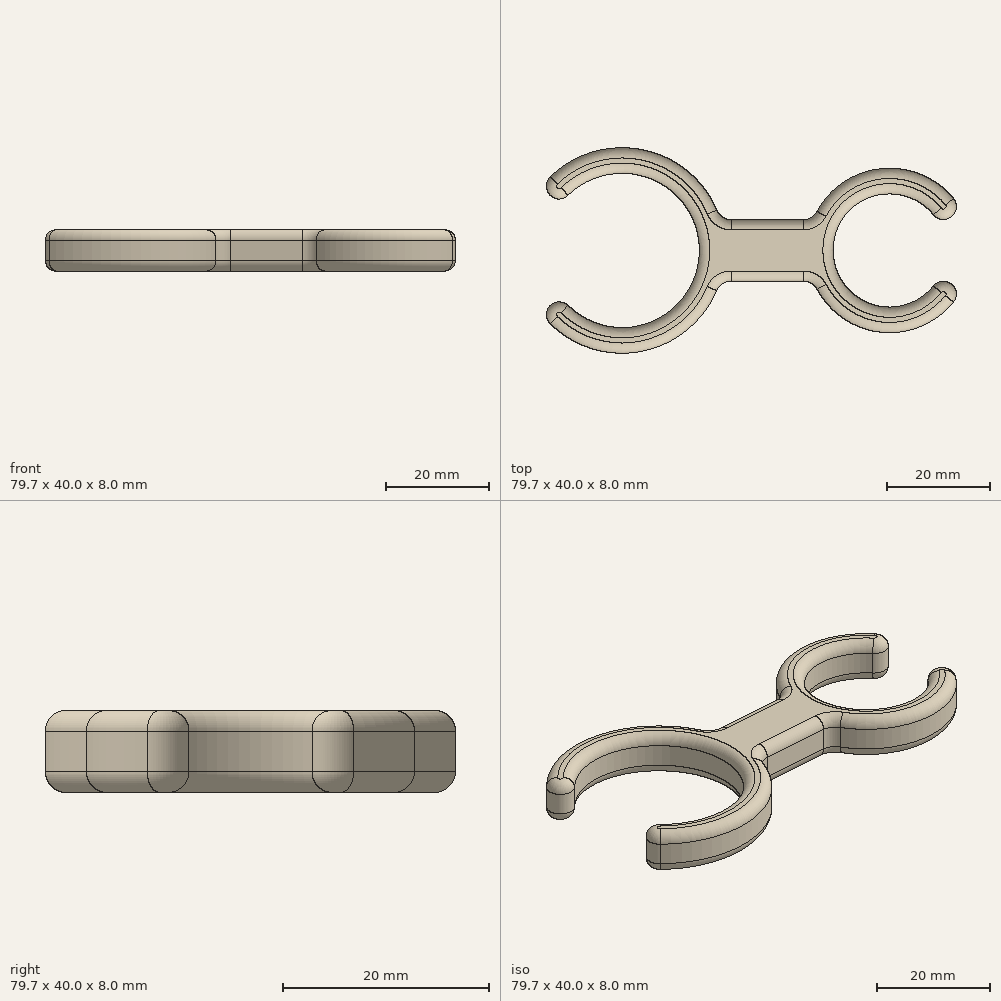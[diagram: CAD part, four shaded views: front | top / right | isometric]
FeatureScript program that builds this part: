
annotation { "Feature Type Name" : "Feature", "Feature Type Description" : "" }
export const myFeature = defineFeature(function(context is Context, id is Id, definition is map)
    precondition{}
    {
        {
            assignVariable(context, id + "F0", {"name" : "ht", "anyValue" : 8});
        }
        {
            var Q0;
            Q0=qCreatedBy(makeId("Top.planeOp"),FACE);
            var sketch = newSketch(context, id + "F1", { "sketchPlane" : qUnion([Q0])});
            skArc(sketch, "E0", {"start": v(-10.5, -10.71) * mm, "mid": v(15, 0) * mm, "end": v(-10.5, 10.71) * mm});
            skArc(sketch, "E1", {"start": v(60.55, 6.93) * mm, "mid": v(41, 0) * mm, "end": v(60.55, -6.93) * mm});
            skLineSegment(sketch, "E2", {"start": v(0, 0) * mm, "end": v(52, 0) * mm, "construction": true});
            skLineSegment(sketch, "E3", {"start": v(19.08, 6) * mm, "end": v(37.17, 6) * mm});
            skLineSegment(sketch, "E4.MirrorCS", {"start": v(19.08, -6) * mm, "end": v(37.17, -6) * mm});
            skArc(sketch, "E5", {"start": v(-14, -14.29) * mm, "mid": v(4.86, -19.4) * mm, "end": v(19.08, -6) * mm});
            skArc(sketch, "E6", {"start": v(64.43, 10.07) * mm, "mid": v(49.64, 15.82) * mm, "end": v(37.17, 6) * mm});
            skArc(sketch, "E7", {"start": v(-14, 14.29) * mm, "mid": v(-14.03, 10.75) * mm, "end": v(-10.5, 10.71) * mm});
            skArc(sketch, "E8.MirrorC", {"start": v(-14, -14.29) * mm, "mid": v(-14.03, -10.75) * mm, "end": v(-10.5, -10.71) * mm});
            skArc(sketch, "E9.trimOffspring", {"start": v(19.08, 6) * mm, "mid": v(4.86, 19.4) * mm, "end": v(-14, 14.29) * mm});
            skPoint(sketch, "E10.orphan", {"position": v(13.75, 6) * mm});
            skPoint(sketch, "E11.orphan", {"position": v(13.75, -6) * mm});
            skArc(sketch, "E12", {"start": v(60.55, 6.93) * mm, "mid": v(64.06, 6.56) * mm, "end": v(64.43, 10.07) * mm});
            skArc(sketch, "E13.MirrorC", {"start": v(60.55, -6.93) * mm, "mid": v(64.06, -6.56) * mm, "end": v(64.43, -10.07) * mm});
            skArc(sketch, "E14.trimOffspring", {"start": v(37.17, -6) * mm, "mid": v(49.64, -15.82) * mm, "end": v(64.43, -10.07) * mm});
            skPoint(sketch, "E15.orphan", {"position": v(42.78, 6) * mm});
            skPoint(sketch, "E16.orphan", {"position": v(42.78, -6) * mm});
            skSolve(sketch);
        }
        {
            var Q0;
            Q0=makeQuery(id+"F1.imprint","IMPRINT",FACE,{"disambiguationData":[TD([[makeQuery(id+"F1.imprint","IMPRINT",EDGE,{"derivedFrom":sQuery(id+"F1.wireOp",EDGE,"E0")}),-1.0]])]});
            extrude(context, id + "F2", {"entities" : qUnion([Q0]), "depth" : (getVariable(context, 'ht')) * mm});
        }
        {
            var Q0;
            Q0=makeQuery(id+"F2.opExtrude","SWEPT_EDGE",EDGE,{"disambiguationData":[OSD([sQuery(id+"F1.wireOp",EDGE,"E4.MirrorCS"),sQuery(id+"F1.wireOp",EDGE,"E5")])]});
            var Q1;
            Q1=makeQuery(id+"F2.opExtrude","SWEPT_EDGE",EDGE,{"disambiguationData":[OSD([sQuery(id+"F1.wireOp",EDGE,"E4.MirrorCS"),sQuery(id+"F1.wireOp",EDGE,"E14.trimOffspring")])]});
            var Q2;
            Q2=makeQuery(id+"F2.opExtrude","SWEPT_EDGE",EDGE,{"disambiguationData":[OSD([sQuery(id+"F1.wireOp",EDGE,"E3"),sQuery(id+"F1.wireOp",EDGE,"E9.trimOffspring")])]});
            var Q3;
            Q3=makeQuery(id+"F2.opExtrude","SWEPT_EDGE",EDGE,{"disambiguationData":[OSD([sQuery(id+"F1.wireOp",EDGE,"E3"),sQuery(id+"F1.wireOp",EDGE,"E6")])]});
            fillet(context, id + "F3", {"entities" : qUnion([Q0, Q1, Q2, Q3]), "radius" : 3 * mm, "tangentPropagation" : true, "allowEdgeOverflow" : false});
        }
        {
            var Q0;
            Q0=makeQuery(id+"F2.opExtrude","CAP_FACE",FACE,{"disambiguationData":[OSD([sQuery(id+"F1.wireOp",EDGE,"E0"),sQuery(id+"F1.wireOp",EDGE,"E1"),sQuery(id+"F1.wireOp",EDGE,"E3"),sQuery(id+"F1.wireOp",EDGE,"E4.MirrorCS"),sQuery(id+"F1.wireOp",EDGE,"E5"),sQuery(id+"F1.wireOp",EDGE,"E6"),sQuery(id+"F1.wireOp",EDGE,"E7"),sQuery(id+"F1.wireOp",EDGE,"E8.MirrorC"),sQuery(id+"F1.wireOp",EDGE,"E9.trimOffspring"),sQuery(id+"F1.wireOp",EDGE,"E12"),sQuery(id+"F1.wireOp",EDGE,"E13.MirrorC"),sQuery(id+"F1.wireOp",EDGE,"E14.trimOffspring")])],"isStart":false});
            var Q1;
            Q1=makeQuery(id+"F2.opExtrude","CAP_FACE",FACE,{"disambiguationData":[OSD([sQuery(id+"F1.wireOp",EDGE,"E0"),sQuery(id+"F1.wireOp",EDGE,"E1"),sQuery(id+"F1.wireOp",EDGE,"E3"),sQuery(id+"F1.wireOp",EDGE,"E4.MirrorCS"),sQuery(id+"F1.wireOp",EDGE,"E5"),sQuery(id+"F1.wireOp",EDGE,"E6"),sQuery(id+"F1.wireOp",EDGE,"E7"),sQuery(id+"F1.wireOp",EDGE,"E8.MirrorC"),sQuery(id+"F1.wireOp",EDGE,"E9.trimOffspring"),sQuery(id+"F1.wireOp",EDGE,"E12"),sQuery(id+"F1.wireOp",EDGE,"E13.MirrorC"),sQuery(id+"F1.wireOp",EDGE,"E14.trimOffspring")])],"isStart":true});
            fillet(context, id + "F4", {"entities" : qUnion([Q0, Q1]), "radius" : 2 * mm, "tangentPropagation" : true, "allowEdgeOverflow" : false});
        }
    });
